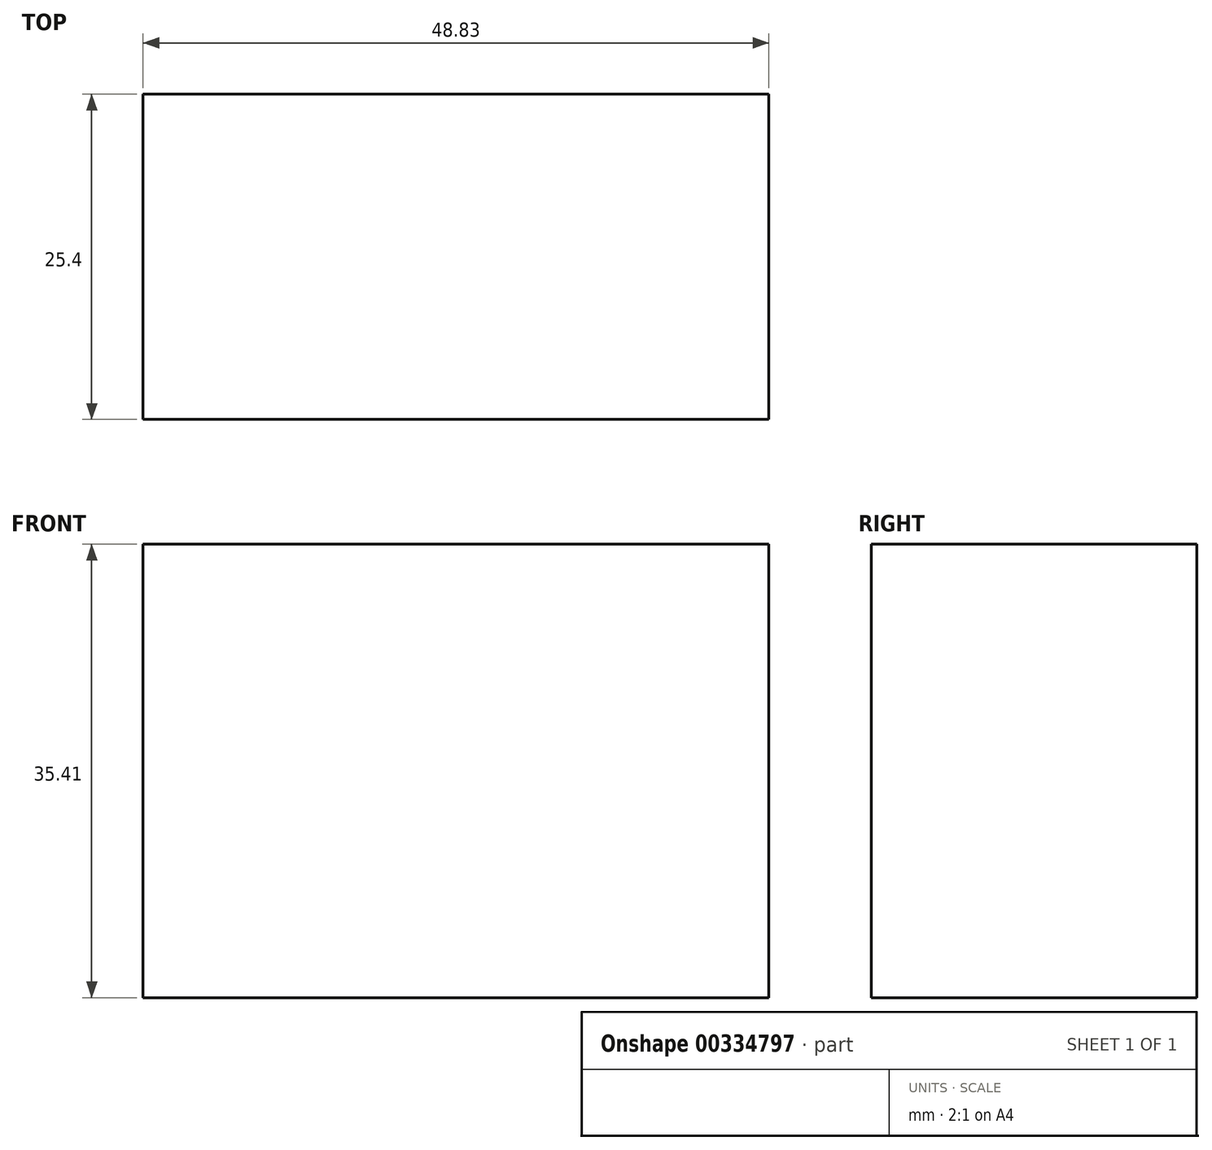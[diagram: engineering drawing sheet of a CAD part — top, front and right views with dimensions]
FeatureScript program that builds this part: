
annotation { "Feature Type Name" : "Feature", "Feature Type Description" : "" }
export const myFeature = defineFeature(function(context is Context, id is Id, definition is map)
    precondition{}
    {
        {
            var Q0;
            Q0=qCreatedBy(makeId("Front.planeOp"),FACE);
            var sketch = newSketch(context, id + "F0", { "sketchPlane" : qUnion([Q0])});
            skLineSegment(sketch, "E0.bottom", {"start": v(-14.85, 14.28) * mm, "end": v(33.98, 14.28) * mm});
            skLineSegment(sketch, "E0.top", {"start": v(-14.85, -21.13) * mm, "end": v(33.98, -21.13) * mm});
            skLineSegment(sketch, "E0.left", {"start": v(-14.85, 14.28) * mm, "end": v(-14.85, -21.13) * mm});
            skLineSegment(sketch, "E0.right", {"start": v(33.98, 14.28) * mm, "end": v(33.98, -21.13) * mm});
            skSolve(sketch);
        }
        {
            var Q0;
            Q0 = qSketchRegion(id + "F0", true);
            extrude(context, id + "F1", {"entities" : qUnion([Q0]), "depth" : 25.4 * mm});
        }
    });
